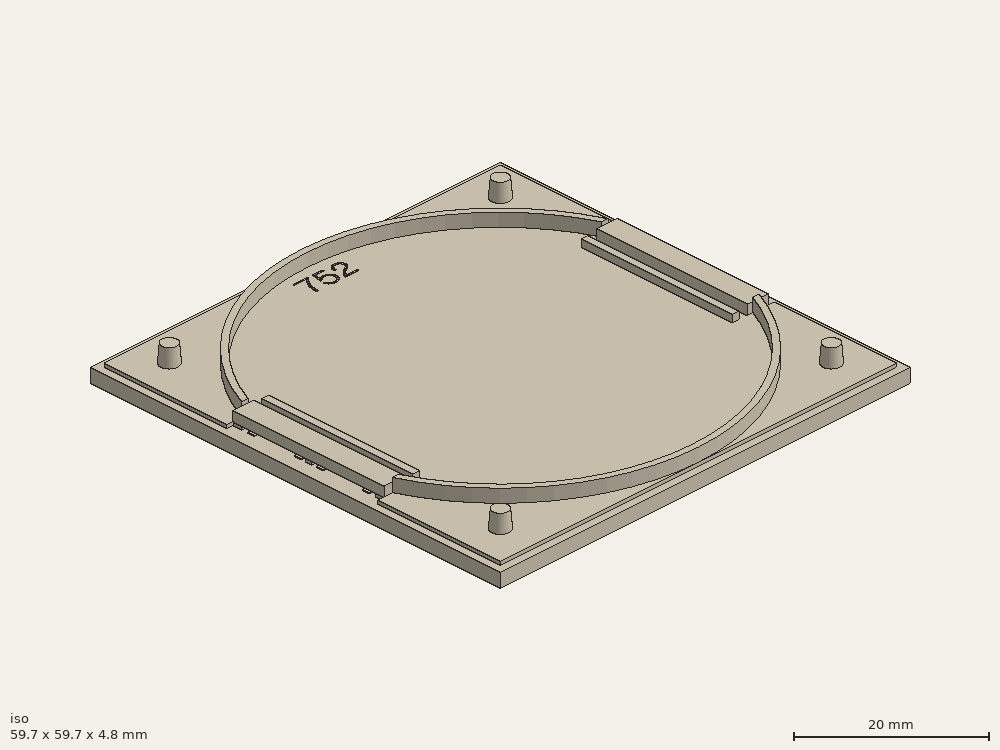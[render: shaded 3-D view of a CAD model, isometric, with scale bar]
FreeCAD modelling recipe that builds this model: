
FCSTD DOCUMENT  (FreeCAD 0.16R)
Label: edizio_part_752
License: All rights reserved
LicenseURL: http://en.wikipedia.org/wiki/All_rights_reserved
objects: Part::Box×24, Part::Cut×5, Part::Cone×4, Part::Cylinder×2, Part::Part2DObjectPython×1, Part::Extrusion×1, Part::FeaturePython×1
note: 38 computed .brp shape members not serialized (recipe doc carries the construction recipe); baked Part::Feature solids carry a one-line shape summary decoded from their .brp

FEATURE [Part::Box] Box  label="Front"
  Height = 1.9
  Length = 59.7
  Width = 59.7
FEATURE [Part::Box] Box001  label="Layer_Inside_Base"
  Height = 0.5
  Length = 57.7
  Placement = pos=(1,1,1.9) rot=(0,0,1;0rad)
  Width = 57.7
FEATURE [Part::Cylinder] Cylinder  label="Cylinder_Outside"
  Angle = 360
  Height = 1.8
  Placement = pos=(29.85,29.85,2.4) rot=(0,0,1;0rad)
  Radius = 28.85
FEATURE [Part::Cylinder] Cylinder001  label="Cylinder_Inside"
  Angle = 360
  Height = 1.8
  Placement = pos=(29.85,29.85,2.4) rot=(0,0,1;0rad)
  Radius = 28
FEATURE [Part::Cut] Cut  label="Cylinder_Base"
  Base = -> Cylinder
  Tool = -> Cylinder001
FEATURE [Part::Cone] Cone  label="Cone_001"
  Angle = 360
  Height = 2.4
  Placement = pos=(5.8,5.8,2.4) rot=(0,0,1;0rad)
  Radius1 = 1.25
  Radius2 = 1.05
FEATURE [Part::Cone] Cone001  label="Cone_002"
  Angle = 360
  Height = 2.4
  Placement = pos=(54,5.8,2.4) rot=(0,0,1;0rad)
  Radius1 = 1.25
  Radius2 = 1.05
FEATURE [Part::Cone] Cone002  label="Cone_003"
  Angle = 360
  Height = 2.4
  Placement = pos=(54,54,2.4) rot=(0,0,1;0rad)
  Radius1 = 1.25
  Radius2 = 1.05
FEATURE [Part::Cone] Cone003  label="Cone_004"
  Angle = 360
  Height = 2.4
  Placement = pos=(5.8,54,2.4) rot=(0,0,1;0rad)
  Radius1 = 1.25
  Radius2 = 1.05
FEATURE [Part::Box] Box002  label="Cut_001"
  Height = 2.5
  Length = 5
  Placement = pos=(0,18.85,1.9) rot=(0,0,1;0rad)
  Width = 22
FEATURE [Part::Box] Box003  label="Cut_002"
  Height = 2.5
  Length = 5
  Placement = pos=(54.7,18.85,1.9) rot=(0,0,1;0rad)
  Width = 22
FEATURE [Part::Cut] Cut001  label="Cylinder_Cut001"
  Base = -> Cut
  Tool = -> Box002
FEATURE [Part::Cut] Cut002  label="Cylinder"
  Base = -> Cut001
  Tool = -> Box003
FEATURE [Part::Box] Box004  label="Cut_003"
  Height = 1.9
  Length = 5
  Placement = pos=(0,18.85,1.9) rot=(0,0,1;0rad)
  Width = 22
FEATURE [Part::Box] Box005  label="Cut_004"
  Height = 1.9
  Length = 5
  Placement = pos=(54.7,18.85,1.9) rot=(0,0,1;0rad)
  Width = 22
FEATURE [Part::Cut] Cut003  label="Layer_Inside_Cut003"
  Base = -> Box001
  Tool = -> Box004
FEATURE [Part::Cut] Cut004  label="Layer_Inside"
  Base = -> Cut003
  Tool = -> Box005
FEATURE [Part::Box] Box006  label="Cube_001"
  Height = 0.1
  Length = 1
  Placement = pos=(1.9,21,1.9) rot=(0,0,1;0rad)
  Width = 1
FEATURE [Part::Box] Box007  label="Cube_002"
  Height = 0.1
  Length = 1
  Placement = pos=(1.9,27.7,1.9) rot=(0,0,1;0rad)
  Width = 1
FEATURE [Part::Box] Box008  label="Cube_003"
  Height = 0.1
  Length = 1
  Placement = pos=(1.9,30.9,1.9) rot=(0,0,1;0rad)
  Width = 1
FEATURE [Part::Box] Box009  label="Cube_004"
  Height = 0.1
  Length = 1
  Placement = pos=(1.9,37.7,1.9) rot=(0,0,1;0rad)
  Width = 1
FEATURE [Part::Box] Box010  label="Cube_005"
  Height = 0.1
  Length = 1
  Placement = pos=(56.8,21,1.9) rot=(0,0,1;0rad)
  Width = 1
FEATURE [Part::Box] Box011  label="Cube_006"
  Height = 0.1
  Length = 1
  Placement = pos=(56.8,27.7,1.9) rot=(0,0,1;0rad)
  Width = 1
FEATURE [Part::Box] Box012  label="Cube_007"
  Height = 0.1
  Length = 1
  Placement = pos=(56.8,30.9,1.9) rot=(0,0,1;0rad)
  Width = 1
FEATURE [Part::Box] Box013  label="Cube_008"
  Height = 0.1
  Length = 1
  Placement = pos=(56.8,37.7,1.9) rot=(0,0,1;0rad)
  Width = 1
FEATURE [Part::Box] Box014  label="Cube_011"
  Height = 0.4
  Length = 3
  Placement = pos=(1.9,18.85,1.9) rot=(0,0,1;0rad)
  Width = 1.3
FEATURE [Part::Box] Box015  label="Cube_012"
  Height = 0.4
  Length = 3
  Placement = pos=(54.9,18.85,1.9) rot=(0,0,1;0rad)
  Width = 1.3
FEATURE [Part::Box] Box016  label="Cube_013"
  Height = 0.4
  Length = 3
  Placement = pos=(1.9,39.55,1.9) rot=(0,0,1;0rad)
  Width = 1.3
FEATURE [Part::Box] Box017  label="Cube_014"
  Height = 0.4
  Length = 3
  Placement = pos=(54.9,39.55,1.9) rot=(0,0,1;0rad)
  Width = 1.3
FEATURE [Part::Box] Box018  label="Cube_015"
  Height = 0.4
  Length = 3
  Placement = pos=(1.9,29.35,1.9) rot=(0,0,1;0rad)
  Width = 1
FEATURE [Part::Box] Box019  label="Cube_016"
  Height = 0.4
  Length = 3
  Placement = pos=(54.9,29.35,1.9) rot=(0,0,1;0rad)
  Width = 1
FEATURE [Part::Box] Box020  label="Cube_021"
  Height = 1.4
  Length = 3
  Placement = pos=(1.9,18.85,2.3) rot=(0,0,1;0rad)
  Width = 22
FEATURE [Part::Box] Box021  label="Cube_022"
  Height = 1.4
  Length = 3
  Placement = pos=(54.86,18.85,2.3) rot=(0,0,1;0rad)
  Width = 22
FEATURE [Part::Box] Box022  label="Cube_031"
  Height = 1
  Length = 1
  Placement = pos=(6.1,18.85,2.4) rot=(0,0,1;0rad)
  Width = 22
FEATURE [Part::Box] Box023  label="Cube_032"
  Height = 1
  Length = 1
  Placement = pos=(52.6,18.85,2.4) rot=(0,0,1;0rad)
  Width = 22
FEATURE [Part::Part2DObjectPython] ShapeString  # Draft 2D object (typed FeaturePython)
  FontFile = <path>
  Size = 0.1
  String = 752
  Tracking = 0
FEATURE [Part::Extrusion] Extrude001
  Base = -> ShapeString
  Dir = (0,0,0.1)
  Placement = pos=(0,0,1.9) rot=(0,0,1;0rad)
  Solid = true
FEATURE [Part::FeaturePython] Scale  # Draft clone (typed FeaturePython)
  Objects = -> [Extrude001]
  Placement = pos=(25.9,53.5,4.4) rot=(0,0,1;0rad)
  Scale = (22,22,0)
note: 1 file-system path scrubbed to <path> (originals preserved in the JSON sidecar)
